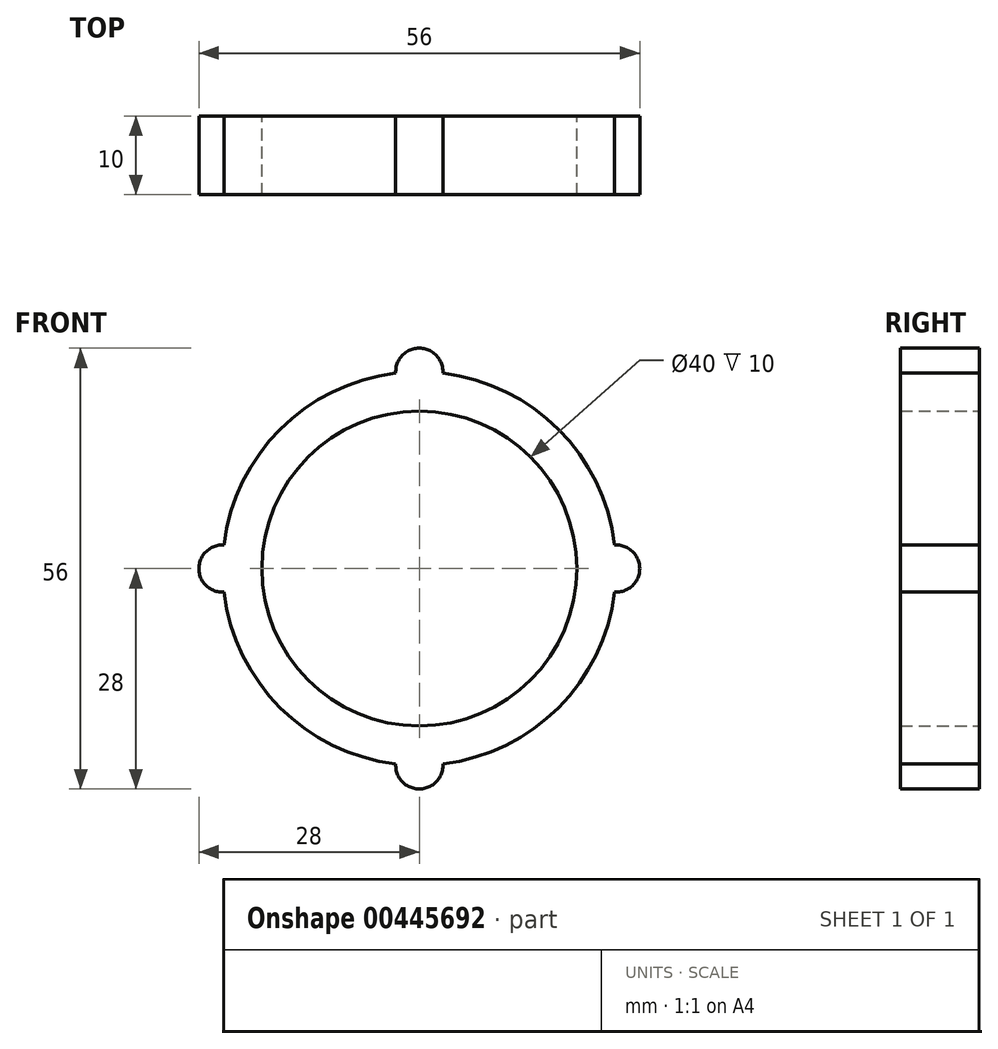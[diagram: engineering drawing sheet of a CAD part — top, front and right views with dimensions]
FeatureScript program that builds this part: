
annotation { "Feature Type Name" : "Feature", "Feature Type Description" : "" }
export const myFeature = defineFeature(function(context is Context, id is Id, definition is map)
    precondition{}
    {
        {
            var Q0;
            Q0=qCreatedBy(makeId("Front.planeOp"),FACE);
            var sketch = newSketch(context, id + "F0", { "sketchPlane" : qUnion([Q0])});
            skLineSegment(sketch, "E0", {"start": v(0, 36.71) * mm, "end": v(0, -32.17) * mm});
            skLineSegment(sketch, "E1", {"start": v(-34.4, 0) * mm, "end": v(32.58, 0) * mm});
            skArc(sketch, "E2", {"start": v(-3, 24.82) * mm, "mid": v(-17.68, 17.68) * mm, "end": v(-24.82, 3) * mm});
            skArc(sketch, "E3", {"start": v(3, 24.82) * mm, "mid": v(0, 28) * mm, "end": v(-3, 24.82) * mm});
            skArc(sketch, "E4", {"start": v(-24.82, 3) * mm, "mid": v(-28, 0) * mm, "end": v(-24.82, -3) * mm});
            skArc(sketch, "E5", {"start": v(-3, -24.82) * mm, "mid": v(0, -28) * mm, "end": v(3, -24.82) * mm});
            skArc(sketch, "E6", {"start": v(24.82, -3) * mm, "mid": v(28, 0) * mm, "end": v(24.82, 3) * mm});
            skArc(sketch, "E7.trimOffspring", {"start": v(-24.82, -3) * mm, "mid": v(-17.68, -17.68) * mm, "end": v(-3, -24.82) * mm});
            skArc(sketch, "E8.trimOffspring", {"start": v(3, -24.82) * mm, "mid": v(17.68, -17.68) * mm, "end": v(24.82, -3) * mm});
            skArc(sketch, "E9.trimOffspring", {"start": v(24.82, 3) * mm, "mid": v(17.68, 17.68) * mm, "end": v(3, 24.82) * mm});
            skCircle(sketch, "E10", {"center": v(0, 0) * mm, "radius": 20 * mm});
            skSolve(sketch);
        }
        {
            var Q0;
            {var subQ0=sQuery(id+"F0.wireOp",EDGE,"E2");Q0=makeQuery(id+"F0.imprint","IMPRINT",FACE,{"disambiguationData":[TD([[makeQuery(id+"F0.imprint","IMPRINT",EDGE,{"derivedFrom":subQ0}),1.0]])]});}
            var Q1;
            {var subQ0=sQuery(id+"F0.wireOp",EDGE,"E7.trimOffspring");Q1=makeQuery(id+"F0.imprint","IMPRINT",FACE,{"disambiguationData":[TD([[makeQuery(id+"F0.imprint","IMPRINT",EDGE,{"derivedFrom":subQ0}),1.0]])]});}
            var Q2;
            {var subQ0=sQuery(id+"F0.wireOp",EDGE,"E8.trimOffspring");Q2=makeQuery(id+"F0.imprint","IMPRINT",FACE,{"disambiguationData":[TD([[makeQuery(id+"F0.imprint","IMPRINT",EDGE,{"derivedFrom":subQ0}),1.0]])]});}
            var Q3;
            {var subQ0=sQuery(id+"F0.wireOp",EDGE,"E9.trimOffspring");Q3=makeQuery(id+"F0.imprint","IMPRINT",FACE,{"disambiguationData":[TD([[makeQuery(id+"F0.imprint","IMPRINT",EDGE,{"derivedFrom":subQ0}),1.0]])]});}
            extrude(context, id + "F1", {"entities" : qUnion([Q0, Q1, Q2, Q3]), "depth" : 10 * mm});
        }
    });
